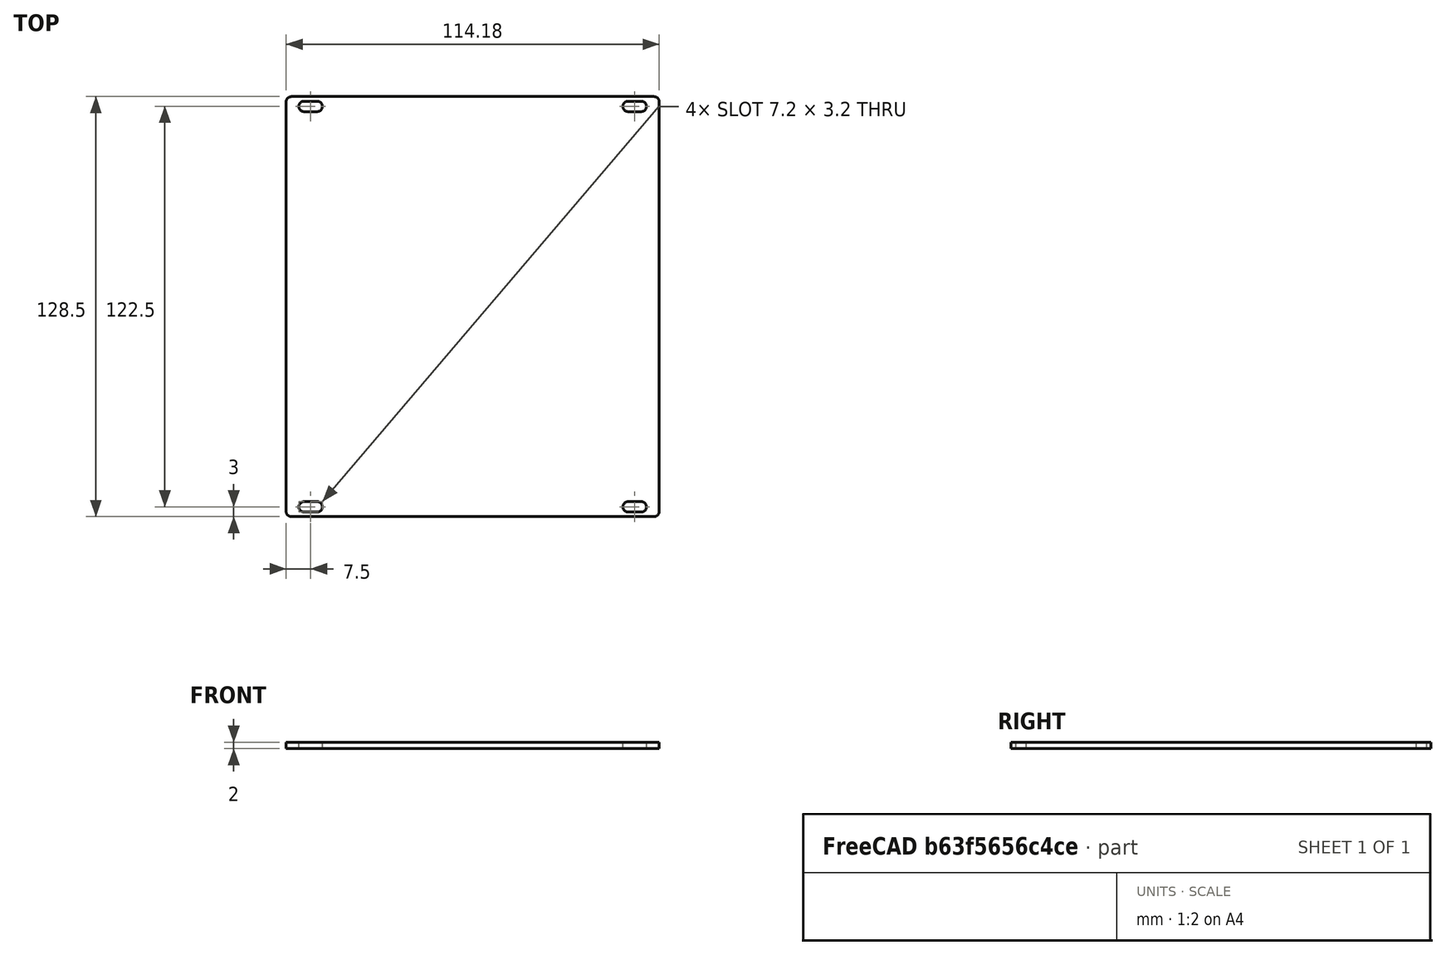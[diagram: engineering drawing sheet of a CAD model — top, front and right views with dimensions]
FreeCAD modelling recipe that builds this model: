
FCSTD DOCUMENT  (FreeCAD 0.19R18543 (Git))
Label: eurorack
License: All rights reserved
LicenseURL: http://en.wikipedia.org/wiki/All_rights_reserved
objects: Sketcher::SketchObject×1, Part::Extrusion×1
note: 2 computed .brp shape members not serialized (recipe doc carries the construction recipe); baked Part::Feature solids carry a one-line shape summary decoded from their .brp

FEATURE [Sketcher::SketchObject] Sketch
  sketch-geometry (40):
    g0: LineSegment StartX=-55.49 StartY=64.25 StartZ=0 EndX=55.49 EndY=64.25 EndZ=0
    g1: LineSegment StartX=57.09 StartY=62.65 StartZ=0 EndX=57.09 EndY=-62.65 EndZ=0
    g2: LineSegment StartX=55.49 StartY=-64.25 StartZ=0 EndX=-55.49 EndY=-64.25 EndZ=0
    g3: LineSegment StartX=-57.09 StartY=-62.65 StartZ=0 EndX=-57.09 EndY=62.65 EndZ=0
    g4: ArcOfCircle CenterX=-55.49 CenterY=62.65 CenterZ=0 NormalX=0 NormalY=0 NormalZ=1 AngleXU=0 Radius=1.6 StartAngle=1.5708 EndAngle=3.14159
    g5: ArcOfCircle CenterX=55.49 CenterY=62.65 CenterZ=0 NormalX=0 NormalY=0 NormalZ=1 AngleXU=0 Radius=1.6 StartAngle=-9e-16 EndAngle=1.5708
    g6: ArcOfCircle CenterX=-55.49 CenterY=-62.65 CenterZ=0 NormalX=0 NormalY=0 NormalZ=1 AngleXU=0 Radius=1.6 StartAngle=3.14159 EndAngle=4.71239
    g7: ArcOfCircle CenterX=55.49 CenterY=-62.65 CenterZ=0 NormalX=0 NormalY=0 NormalZ=1 AngleXU=0 Radius=1.6 StartAngle=4.71239 EndAngle=6.28319
    g8: LineSegment [constr] StartX=-57.09 StartY=64.25 StartZ=0 EndX=57.09 EndY=64.25 EndZ=0
    g9: LineSegment [constr] StartX=57.09 StartY=64.25 StartZ=0 EndX=57.09 EndY=-64.25 EndZ=0
    g10: LineSegment [constr] StartX=57.09 StartY=-64.25 StartZ=0 EndX=-57.09 EndY=-64.25 EndZ=0
    g11: LineSegment [constr] StartX=-57.09 StartY=-64.25 StartZ=0 EndX=-57.09 EndY=64.25 EndZ=0
    g12: ArcOfCircle CenterX=-51.59 CenterY=61.25 CenterZ=0 NormalX=0 NormalY=0 NormalZ=1 AngleXU=0 Radius=1.6 StartAngle=1.5708 EndAngle=4.71239
    g13: ArcOfCircle CenterX=-47.59 CenterY=61.25 CenterZ=0 NormalX=0 NormalY=0 NormalZ=1 AngleXU=0 Radius=1.6 StartAngle=4.71239 EndAngle=7.85398
    g14: LineSegment StartX=-51.59 StartY=59.65 StartZ=0 EndX=-47.59 EndY=59.65 EndZ=0
    g15: LineSegment StartX=-51.59 StartY=62.85 StartZ=0 EndX=-47.59 EndY=62.85 EndZ=0
    g16: LineSegment [constr] StartX=-51.59 StartY=62.85 StartZ=0 EndX=-47.59 EndY=59.65 EndZ=0
    g17: LineSegment [constr] StartX=-51.59 StartY=59.65 StartZ=0 EndX=-47.59 EndY=62.85 EndZ=0
    g18: GeomPoint X=-49.59 Y=61.25 Z=0
    g19: ArcOfCircle CenterX=47.59 CenterY=61.25 CenterZ=0 NormalX=0 NormalY=0 NormalZ=1 AngleXU=0 Radius=1.6 StartAngle=1.5708 EndAngle=4.71239
    g20: ArcOfCircle CenterX=51.59 CenterY=61.25 CenterZ=0 NormalX=0 NormalY=0 NormalZ=1 AngleXU=0 Radius=1.6 StartAngle=4.71239 EndAngle=7.85398
    g21: LineSegment StartX=47.59 StartY=59.65 StartZ=0 EndX=51.59 EndY=59.65 EndZ=0
    g22: LineSegment StartX=47.59 StartY=62.85 StartZ=0 EndX=51.59 EndY=62.85 EndZ=0
    g23: LineSegment [constr] StartX=47.59 StartY=62.85 StartZ=0 EndX=51.59 EndY=59.65 EndZ=0
    g24: LineSegment [constr] StartX=47.59 StartY=59.65 StartZ=0 EndX=51.59 EndY=62.85 EndZ=0
    g25: GeomPoint X=49.59 Y=61.25 Z=0
    g26: ArcOfCircle CenterX=-51.59 CenterY=-61.25 CenterZ=0 NormalX=0 NormalY=0 NormalZ=1 AngleXU=0 Radius=1.6 StartAngle=1.5708 EndAngle=4.71239
    g27: ArcOfCircle CenterX=-47.59 CenterY=-61.25 CenterZ=0 NormalX=0 NormalY=0 NormalZ=1 AngleXU=0 Radius=1.6 StartAngle=4.71239 EndAngle=7.85398
    g28: LineSegment StartX=-51.59 StartY=-62.85 StartZ=0 EndX=-47.59 EndY=-62.85 EndZ=0
    g29: LineSegment StartX=-51.59 StartY=-59.65 StartZ=0 EndX=-47.59 EndY=-59.65 EndZ=0
    g30: LineSegment [constr] StartX=-51.59 StartY=-62.85 StartZ=0 EndX=-47.59 EndY=-59.65 EndZ=0
    g31: LineSegment [constr] StartX=-51.59 StartY=-59.65 StartZ=0 EndX=-47.59 EndY=-62.85 EndZ=0
    g32: GeomPoint X=-49.59 Y=-61.25 Z=0
    g33: ArcOfCircle CenterX=47.59 CenterY=-61.25 CenterZ=0 NormalX=0 NormalY=0 NormalZ=1 AngleXU=0 Radius=1.6 StartAngle=1.5708 EndAngle=4.71239
    g34: ArcOfCircle CenterX=51.59 CenterY=-61.25 CenterZ=0 NormalX=0 NormalY=0 NormalZ=1 AngleXU=0 Radius=1.6 StartAngle=4.71239 EndAngle=7.85398
    g35: LineSegment StartX=47.59 StartY=-62.85 StartZ=0 EndX=51.59 EndY=-62.85 EndZ=0
    g36: LineSegment StartX=47.59 StartY=-59.65 StartZ=0 EndX=51.59 EndY=-59.65 EndZ=0
    g37: LineSegment [constr] StartX=47.59 StartY=-59.65 StartZ=0 EndX=51.59 EndY=-62.85 EndZ=0
    g38: LineSegment [constr] StartX=47.59 StartY=-62.85 StartZ=0 EndX=51.59 EndY=-59.65 EndZ=0
    g39: GeomPoint X=49.59 Y=-61.25 Z=0
  constraints (94):
    c: Horizontal(g2)
    c: Vertical(g1)
    c: Tangent(g3,g4) = 1.5708
    c: Tangent(g0,g4) = 1.5708
    c: Tangent(g0,g5) = 1.5708
    c: Tangent(g1,g5) = 1.5708
    c: Tangent(g3,g6) = 1.5708
    c: Tangent(g2,g6) = 1.5708
    c: Tangent(g2,g7) = 1.5708
    c: Tangent(g1,g7) = 1.5708
    c: Radius(g4) = 1.6  'r1'
    c: Equal(g4,g5)
    c: Equal(g4,g7)
    c: Equal(g4,g6)
    c: Horizontal(g0)
    c: Vertical(g3)
    c: Coincident(g8,g9)
    c: Coincident(g9,g10)
    c: Coincident(g10,g11)
    c: Coincident(g11,g8)
    c: Horizontal(g10)
    c: Vertical(g9)
    c: Symmetric(g8,g10,g-1)
    c: Symmetric(g8,g8,g-2)
    c: DistanceX(g8,g8) = 114.18  'length'
    c: DistanceY(g9,g8) = 128.5  'height'
    c: Vertical(g3,g10)
    c: Vertical(g1,g9)
    c: Horizontal(g2,g10)
    c: Horizontal(g0,g8)
    c: Tangent(g12,g15) = 1.5708
    c: Tangent(g12,g14) = -1.5708
    c: Tangent(g14,g13) = -1.5708
    c: Tangent(g15,g13) = 1.5708
    c: Horizontal(g14)
    c: Equal(g12,g13)
    c: DistanceY(g12,g8) = 3
    c: Coincident(g16,g12)
    c: Coincident(g16,g13)
    c: Coincident(g17,g12)
    c: Coincident(g17,g13)
    c: PointOnObject(g18,g17)
    c: PointOnObject(g18,g16)
    c: DistanceX(g3,g18) = 7.5
    c: Radius(g12) = 1.6
    c: Tangent(g19,g22) = 1.5708
    c: Tangent(g19,g21) = -1.5708
    c: Tangent(g21,g20) = -1.5708
    c: Tangent(g22,g20) = 1.5708
    c: Horizontal(g21)
    c: Equal(g19,g20)
    c: Coincident(g23,g19)
    c: Coincident(g23,g20)
    c: Coincident(g24,g19)
    c: Coincident(g24,g20)
    c: PointOnObject(g25,g23)
    c: PointOnObject(g25,g24)
    c: Radius(g19) = 1.6
    c: DistanceX(g25,g8) = 7.5
    c: DistanceY(g25,g8) = 3
    c: DistanceX(g21,g21) = 4
    c: DistanceX(g14,g14) = 4
    c: Tangent(g26,g29) = 1.5708
    c: Tangent(g26,g28) = -1.5708
    c: Tangent(g28,g27) = -1.5708
    c: Tangent(g29,g27) = 1.5708
    c: Horizontal(g28)
    c: Equal(g26,g27)
    c: Coincident(g30,g26)
    c: Coincident(g30,g27)
    c: Coincident(g31,g26)
    c: Coincident(g31,g27)
    c: PointOnObject(g32,g30)
    c: PointOnObject(g32,g31)
    c: Radius(g27) = 1.6
    c: DistanceX(g29,g29) = 4
    c: DistanceY(g10,g32) = 3
    c: DistanceX(g10,g32) = 7.5
    c: Tangent(g33,g36) = 1.5708
    c: Tangent(g33,g35) = -1.5708
    c: Tangent(g35,g34) = -1.5708
    c: Tangent(g36,g34) = 1.5708
    c: Horizontal(g35)
    c: Equal(g33,g34)
    c: Coincident(g37,g33)
    c: Coincident(g37,g34)
    c: Coincident(g38,g33)
    c: Coincident(g38,g34)
    c: PointOnObject(g39,g38)
    c: PointOnObject(g39,g37)
    c: Radius(g34) = 1.6
    c: DistanceX(g35,g35) = 4
    c: DistanceY(g9,g39) = 3
    c: DistanceX(g39,g9) = 7.5
FEATURE [Part::Extrusion] Extrude
  Base = -> Sketch
  Dir = (0,0,-1)
  DirMode = 0
  FaceMakerClass = Part::FaceMakerBullseye
  LengthFwd = 2
  LengthRev = 0
  Solid = true
  Symmetric = false
